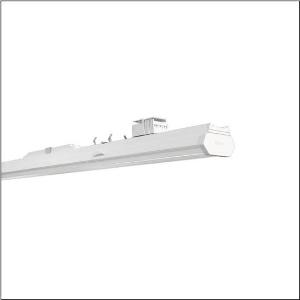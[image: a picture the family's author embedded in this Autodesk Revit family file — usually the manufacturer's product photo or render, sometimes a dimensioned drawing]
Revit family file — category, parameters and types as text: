
# Revit family: licross_r__21_protected_mo_52td11vn48xgd_36f3
name_source: partatom
category: Lighting Fixtures
units: mm (PartAtom-declared; Revit-internal decimal feet)

## family parameters
Cut with Voids When Loaded = No
Host = Face
Light Source = No
Part Type = Normal
Room Calculation Point = No
Round Connector Dimension = Use Diameter
Shared = No

## types (1)
- --- (1 x LED, 980 lm, 7 W, 4000K)
    Apparent Load = 7 VA
    CIE Flux Codes = 83 94 98 100 100
    Color Rendering = 80
    Color Temperature = 4000K
    Default Elevation = 1800 mm
    Description = Licross® 21 Protected MO, luminaire insert, of sheet steel, galvanised, coil coated, white, length: 1.500mm, width: 90mm, height: 103mm, LED rated luminous flux: 8.000lm, light colour: 840, control gear: DALI 2, CLO (for two DALI lines), with plug, 6-pole, with phase selection, mains connection: 220..240V, AC/DC, 0/50..60Hz, start of lifetime: 46W, end of service life: 52W, without changeover relay, for emergency light function, for central battery installations according to DIN EN 60598-2-22, halogen-free wiring, primary optical cover: cover, of PMMA, light emission: direct distribution, primary light characteristic: symmetric, protection rating (complete): IP54, insulation class (complete): insulation class I (protective earthing), certification: CE, ENEC, VDE, UKCA, protection symbol: D if used in an environment with non-conductive dust loads with corresponding accessories, impact resistance: IK06, permissible ambient temperature for indoor applications: -25..+50°C, standard: EN 60598-2-22, corresponds to IFS (International Featured Standards) requirements for safety and quality in the food industry, reducing of maximum allowable ambient temperature of 5°C with ceiling mounting, LABS conformity tested according to VDMA 24364:2018-05, packaging unit: 1 piece
    Height = 92 mm
    Lamp = 1 x LED
    Lamp Light Flux = 980 lm
    Lamp Power = 7 W
    Lamp count = 1
    Length = 1500 mm
    Luminous efficacy = 140 lm/W
    Manufacturer = Siteco
    ModVariant = No
    Model = 52TD11VN48XGD
    Mounting Place = Ceiling
    Mounting Type = Pendant
    Number of Poles = 1
    OnlyDefault = Yes
    Power Factor = 1
    Product Name = Licross® 21 Protected MO
    Product group = luminaire insert
    ProductGroupID = 901
    Protection Class = Protection class I
    Protection Degree = IP 54
    RLX_Detail_Level = 1
    RLX_Emergency_Light_Flux = 0 lm
    RLX_Emergency_Type = 0
    RLX_Emergency_Type_DB = No
    RlxData = <blob elided: 24657 chars, md5=1ef85602>
    Socket = socket
    Standby Power = 0 W
    System Light Flux = 980 lm
    System Power = 7 W
    Type Comments = : DC mode (central or group accumulator) initial emergency light level
    Type Image = l_1256148.jpg
    URL = http://relux.com
    VarID = @adj_051893
    Voltage = 0 V
    Weight = 0.00 kg
    Width = 88 mm

## geometry (parser evidence)
native form markers: Blend x4, Sweep x11
no freeform markers — native parametric forms only
